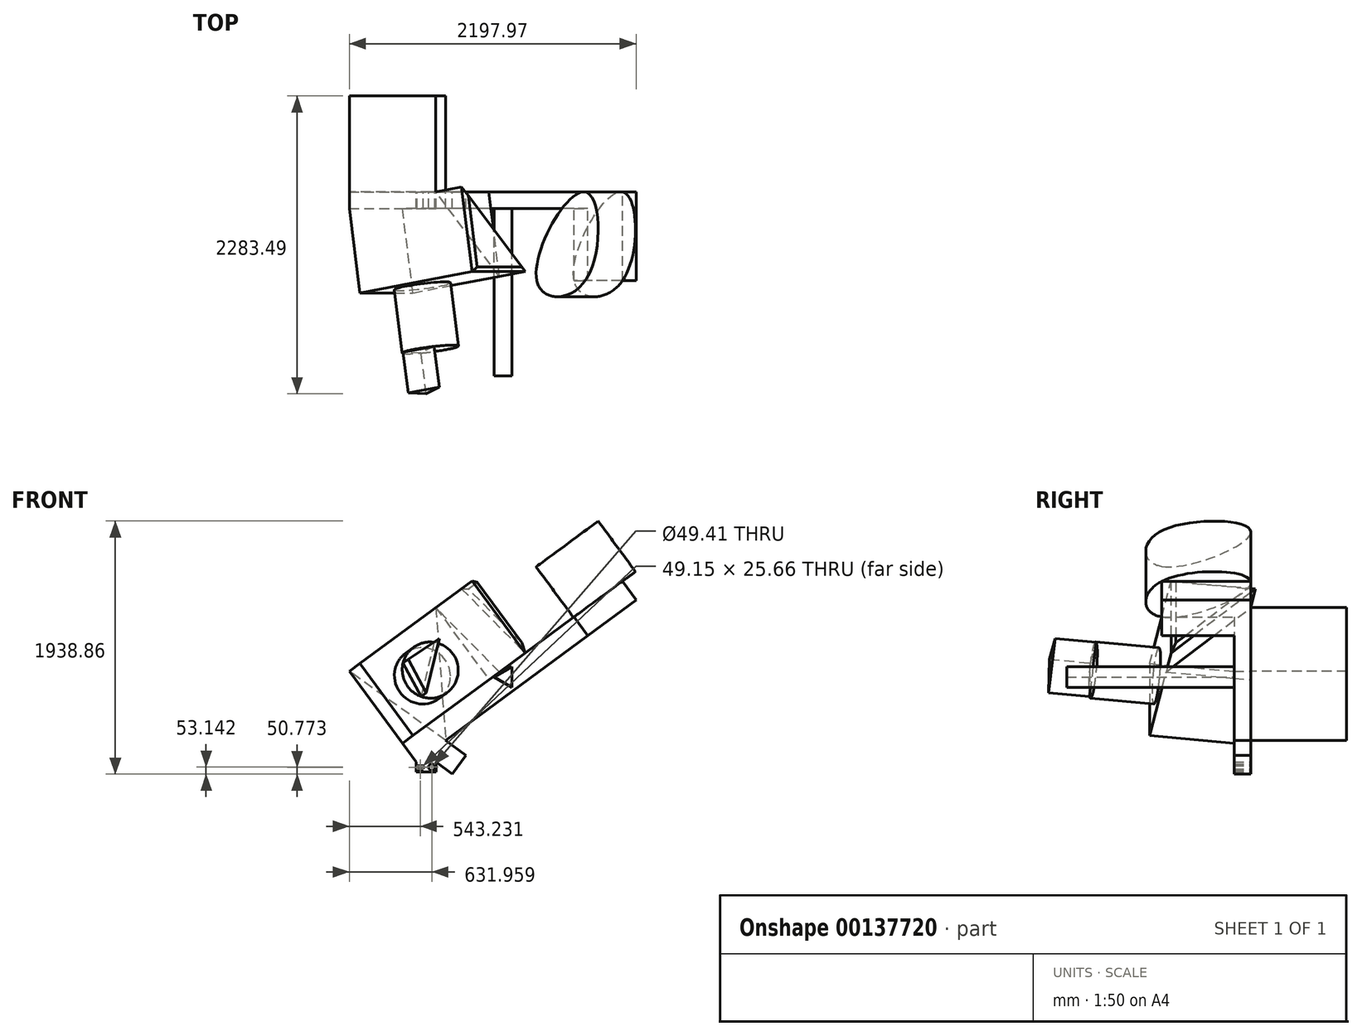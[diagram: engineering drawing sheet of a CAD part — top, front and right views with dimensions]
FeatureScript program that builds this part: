
annotation { "Feature Type Name" : "Feature", "Feature Type Description" : "" }
export const myFeature = defineFeature(function(context is Context, id is Id, definition is map)
    precondition{}
    {
        {
            var Q0;
            Q0=qCreatedBy(makeId("Front.planeOp"),FACE);
            var sketch = newSketch(context, id + "F0", { "sketchPlane" : qUnion([Q0])});
            skLineSegment(sketch, "E0", {"start": v(0, 0) * mm, "end": v(-76.16, 0) * mm});
            skLineSegment(sketch, "E1", {"start": v(-76.16, 0) * mm, "end": v(-76.16, -76.26) * mm});
            skLineSegment(sketch, "E2", {"start": v(-76.16, -76.26) * mm, "end": v(76.16, -76.26) * mm});
            skLineSegment(sketch, "E3", {"start": v(76.16, -76.26) * mm, "end": v(76.16, 0) * mm});
            skLineSegment(sketch, "E4", {"start": v(76.16, 0) * mm, "end": v(0, 0) * mm});
            skLineSegment(sketch, "E5", {"start": v(76.16, 0) * mm, "end": v(0, 56.14) * mm});
            skLineSegment(sketch, "E6", {"start": v(0, 56.14) * mm, "end": v(-76.16, 0) * mm});
            skLineSegment(sketch, "E7", {"start": v(-10.26, -35.22) * mm, "end": v(0, -35.22) * mm});
            skLineSegment(sketch, "E8", {"start": v(0, -35.22) * mm, "end": v(10.26, -35.22) * mm});
            skLineSegment(sketch, "E9", {"start": v(10.26, -35.22) * mm, "end": v(10.26, -76.26) * mm});
            skLineSegment(sketch, "E10", {"start": v(-10.26, -35.22) * mm, "end": v(-10.26, -76.26) * mm});
            skLineSegment(sketch, "E11.bottom", {"start": v(-70.07, -28.36) * mm, "end": v(-20.92, -28.36) * mm});
            skLineSegment(sketch, "E11.top", {"start": v(-70.07, -54.02) * mm, "end": v(-20.92, -54.02) * mm});
            skLineSegment(sketch, "E11.left", {"start": v(-70.07, -28.36) * mm, "end": v(-70.07, -54.02) * mm});
            skLineSegment(sketch, "E11.right", {"start": v(-20.92, -28.36) * mm, "end": v(-20.92, -54.02) * mm});
            skCircle(sketch, "E12", {"center": v(43.23, -38.82) * mm, "radius": 24.7 * mm});
            skSolve(sketch);
        }
        {
            var Q0;
            Q0 = qSketchRegion(id + "F0", true);
            extrude(context, id + "F1", {"entities" : qUnion([Q0]), "depth" : 127 * mm});
        }
        {
            var Q0;
            Q0=makeQuery(id+"F1.opExtrude","SWEPT_FACE",FACE,{"disambiguationData":[OSD([sQuery(id+"F0.wireOp",EDGE,"E5")])]});
            extrude(context, id + "F2", {"entities" : qUnion([Q0]), "operationType" : NewBodyOperationType.ADD, "depth" : 177.8 * mm});
        }
        {
            var Q0;
            Q0=makeQuery(id+"F1.opExtrude","SWEPT_FACE",FACE,{"disambiguationData":[OSD([sQuery(id+"F0.wireOp",EDGE,"E6")])]});
            extrude(context, id + "F3", {"entities" : qUnion([Q0]), "operationType" : NewBodyOperationType.ADD, "depth" : 177.8 * mm});
        }
        {
            var Q0;
            Q0=makeQuery(id+"F3.opExtrude","SWEPT_FACE",FACE,{"disambiguationData":[OSD([sQuery(id+"F0.wireOp",EDGE,"E5"),sQuery(id+"F0.wireOp",EDGE,"E6")])]});
            extrude(context, id + "F4", {"entities" : qUnion([Q0]), "operationType" : NewBodyOperationType.ADD, "depth" : 296.86 * mm});
        }
        {
            var Q0;
            Q0=makeQuery(id+"F2.opExtrude","SWEPT_FACE",FACE,{"disambiguationData":[OSD([sQuery(id+"F0.wireOp",EDGE,"E3"),sQuery(id+"F0.wireOp",EDGE,"E4"),sQuery(id+"F0.wireOp",EDGE,"E5")])]});
            extrude(context, id + "F5", {"entities" : qUnion([Q0]), "operationType" : NewBodyOperationType.ADD, "depth" : 155 * mm});
        }
        {
            var Q0;
            Q0=makeQuery(id+"F4.opExtrude","CAP_FACE",FACE,{"disambiguationData":[OSD([sQuery(id+"F0.wireOp",EDGE,"E5"),sQuery(id+"F0.wireOp",EDGE,"E6")])],"isStart":false});
            extrude(context, id + "F6", {"entities" : qUnion([Q0]), "operationType" : NewBodyOperationType.ADD, "depth" : 1702.25 * mm});
        }
        {
            var Q0;
            {var subQ0=sQuery(id+"F0.wireOp",EDGE,"E6");var subQ1=sQuery(id+"F0.wireOp",EDGE,"E5");var subQ2=makeQuery(id+"F1.opExtrude","CAP_VERTEX",VERTEX,{"disambiguationData":[OSD([subQ1,subQ0])],"isStart":false});var subQ3=makeQuery(id+"F3.opExtrude","SWEPT_EDGE",EDGE,{"disambiguationData":[OSD([subQ1,subQ0]),TDD([makeQuery(id+"F2.boolean.opBoolean","MERGE",VERTEX,{"derivedFrom":[subQ2,makeQuery(id+"F2.opExtrude","CAP_VERTEX",VERTEX,{"disambiguationData":[OSD([subQ1,subQ0]),TDD([subQ2])],"isStart":true})]})])]});var subQ4=sQuery(id+"F0.wireOp",EDGE,"E4");var subQ5=sQuery(id+"F0.wireOp",EDGE,"E3");Q0=makeQuery(id+"F6.boolean.opBoolean","MERGE",FACE,{"derivedFrom":[makeQuery(id+"F5.boolean.opBoolean","MERGE",FACE,{"derivedFrom":[makeQuery(id+"F4.boolean.opBoolean","MERGE",FACE,{"derivedFrom":[makeQuery(id+"F3.boolean.opBoolean","MERGE",FACE,{"derivedFrom":[makeQuery(id+"F2.boolean.opBoolean","MERGE",FACE,{"derivedFrom":[makeQuery(id+"F1.opExtrude","CAP_FACE",FACE,{"disambiguationData":[OSD([sQuery(id+"F0.wireOp",EDGE,"E1"),sQuery(id+"F0.wireOp",EDGE,"E2"),subQ5,subQ1,subQ0,sQuery(id+"F0.wireOp",EDGE,"E11.bottom"),sQuery(id+"F0.wireOp",EDGE,"E11.top"),sQuery(id+"F0.wireOp",EDGE,"E11.left"),sQuery(id+"F0.wireOp",EDGE,"E11.right"),sQuery(id+"F0.wireOp",EDGE,"E12")])],"isStart":false}),makeQuery(id+"F2.opExtrude","SWEPT_FACE",FACE,{"disambiguationData":[OSD([subQ1]),TDD([makeQuery(id+"F1.opExtrude","CAP_EDGE",EDGE,{"disambiguationData":[OSD([subQ1])],"isStart":false})])]})]}),makeQuery(id+"F3.opExtrude","SWEPT_FACE",FACE,{"disambiguationData":[OSD([subQ0]),TDD([makeQuery(id+"F1.opExtrude","CAP_EDGE",EDGE,{"disambiguationData":[OSD([subQ0])],"isStart":false})])]})]}),makeQuery(id+"F4.opExtrude","SWEPT_FACE",FACE,{"disambiguationData":[OSD([subQ1,subQ0]),TDD([subQ3])]})]}),makeQuery(id+"F5.opExtrude","SWEPT_FACE",FACE,{"disambiguationData":[OSD([subQ5,subQ4,subQ1]),TDD([makeQuery(id+"F2.opExtrude","SWEPT_EDGE",EDGE,{"disambiguationData":[OSD([subQ5,subQ4,subQ1]),TDD([makeQuery(id+"F1.opExtrude","CAP_VERTEX",VERTEX,{"disambiguationData":[OSD([subQ5,subQ4,subQ1])],"isStart":false})])]})])]})]}),makeQuery(id+"F6.opExtrude","SWEPT_FACE",FACE,{"disambiguationData":[OSD([subQ1,subQ0]),TDD([makeQuery(id+"F4.opExtrude","CAP_EDGE",EDGE,{"disambiguationData":[OSD([subQ1,subQ0]),TDD([subQ3])],"isStart":false})])]})]});}
            var sketch = newSketch(context, id + "F7", { "sketchPlane" : qUnion([Q0])});
            skLineSegment(sketch, "E13", {"start": v(1134, 1112.82) * mm, "end": v(1239.5, 969.7) * mm});
            skLineSegment(sketch, "E14", {"start": v(1134, 1112.82) * mm, "end": v(1503.75, 1385.34) * mm});
            skLineSegment(sketch, "E15", {"start": v(1503.75, 1385.34) * mm, "end": v(1609.24, 1242.22) * mm});
            skLineSegment(sketch, "E16", {"start": v(1609.24, 1242.22) * mm, "end": v(1239.5, 969.7) * mm});
            skSolve(sketch);
        }
        {
            var Q0;
            Q0 = qSketchRegion(id + "F7", true);
            extrude(context, id + "F8", {"entities" : qUnion([Q0]), "operationType" : NewBodyOperationType.ADD, "depth" : 554.12 * mm});
        }
        {
            var Q0;
            {var subQ0=sQuery(id+"F0.wireOp",EDGE,"E6");var subQ1=sQuery(id+"F0.wireOp",EDGE,"E5");var subQ2=makeQuery(id+"F3.opExtrude","CAP_EDGE",EDGE,{"disambiguationData":[OSD([subQ1,subQ0])],"isStart":false});Q0=makeQuery(id+"F8.boolean.opBoolean","MERGE",FACE,{"derivedFrom":[makeQuery(id+"F6.boolean.opBoolean","MERGE",FACE,{"derivedFrom":[makeQuery(id+"F4.boolean.opBoolean","MERGE",FACE,{"derivedFrom":[makeQuery(id+"F3.opExtrude","CAP_FACE",FACE,{"disambiguationData":[OSD([subQ0])],"isStart":false}),makeQuery(id+"F4.opExtrude","SWEPT_FACE",FACE,{"disambiguationData":[OSD([subQ1,subQ0]),TDD([subQ2])]})]}),makeQuery(id+"F6.opExtrude","SWEPT_FACE",FACE,{"disambiguationData":[OSD([subQ1,subQ0]),TDD([makeQuery(id+"F4.opExtrude","CAP_EDGE",EDGE,{"disambiguationData":[OSD([subQ1,subQ0]),TDD([subQ2])],"isStart":false})])]})]}),makeQuery(id+"F8.opExtrude","SWEPT_FACE",FACE,{"disambiguationData":[OSD([sQuery(id+"F7.wireOp",EDGE,"E14")])]})]});}
            var sketch = newSketch(context, id + "F9", { "sketchPlane" : qUnion([Q0])});
            skLineSegment(sketch, "E17", {"start": v(-61.3, -127) * mm, "end": v(761.56, 0) * mm});
            skLineSegment(sketch, "E18", {"start": v(761.56, 0) * mm, "end": v(-61.3, 0) * mm});
            skLineSegment(sketch, "E19", {"start": v(-61.3, 0) * mm, "end": v(-61.3, -127) * mm});
            skSolve(sketch);
        }
        {
            var Q0;
            Q0 = qSketchRegion(id + "F9", true);
            extrude(context, id + "F10", {"entities" : qUnion([Q0]), "operationType" : NewBodyOperationType.ADD, "depth" : 686.12 * mm});
        }
        {
            var Q0;
            Q0=makeQuery(id+"F10.opExtrude","SWEPT_FACE",FACE,{"disambiguationData":[OSD([sQuery(id+"F9.wireOp",EDGE,"E17")])]});
            extrude(context, id + "F11", {"entities" : qUnion([Q0]), "operationType" : NewBodyOperationType.ADD, "depth" : 654.53 * mm});
        }
        {
            var Q0;
            Q0=makeQuery(id+"F11.opExtrude","SWEPT_FACE",FACE,{"disambiguationData":[OSD([sQuery(id+"F0.wireOp",EDGE,"E5"),sQuery(id+"F0.wireOp",EDGE,"E6"),sQuery(id+"F9.wireOp",EDGE,"E17"),sQuery(id+"F9.wireOp",EDGE,"E18")])]});
            var sketch = newSketch(context, id + "F12", { "sketchPlane" : qUnion([Q0])});
            skLineSegment(sketch, "E20", {"start": v(-770.7, 222.99) * mm, "end": v(-116.16, 909.1) * mm});
            skLineSegment(sketch, "E21", {"start": v(-116.16, 909.1) * mm, "end": v(-770.7, 909.1) * mm});
            skLineSegment(sketch, "E22", {"start": v(-770.7, 909.1) * mm, "end": v(-770.7, 222.99) * mm});
            skSolve(sketch);
        }
        {
            var Q0;
            Q0 = qSketchRegion(id + "F12", true);
            extrude(context, id + "F13", {"entities" : qUnion([Q0]), "operationType" : NewBodyOperationType.ADD, "depth" : 278.87 * mm});
        }
        {
            var Q0;
            Q0=makeQuery(id+"F13.boolean.opBoolean","MERGE",FACE,{"derivedFrom":[makeQuery(id+"F11.opExtrude","CAP_FACE",FACE,{"disambiguationData":[OSD([sQuery(id+"F9.wireOp",EDGE,"E17")])],"isStart":false}),makeQuery(id+"F13.opExtrude","SWEPT_FACE",FACE,{"disambiguationData":[OSD([sQuery(id+"F12.wireOp",EDGE,"E22")])]})]});
            var sketch = newSketch(context, id + "F14", { "sketchPlane" : qUnion([Q0])});
            skCircle(sketch, "E23", {"center": v(-124.02, 591.83) * mm, "radius": 216.26 * mm});
            skSolve(sketch);
        }
        {
            var Q0;
            Q0 = qSketchRegion(id + "F14", true);
            extrude(context, id + "F15", {"entities" : qUnion([Q0]), "operationType" : NewBodyOperationType.ADD, "depth" : 490.5 * mm});
        }
        {
            var Q0;
            Q0=makeQuery(id+"F15.opExtrude","CAP_FACE",FACE,{"disambiguationData":[OSD([sQuery(id+"F14.wireOp",EDGE,"E23")])],"isStart":false});
            var sketch = newSketch(context, id + "F16", { "sketchPlane" : qUnion([Q0])});
            skLineSegment(sketch, "E24", {"start": v(-93.59, 805.94) * mm, "end": v(-194.9, 387.5) * mm});
            skLineSegment(sketch, "E25", {"start": v(-194.9, 387.5) * mm, "end": v(-333.83, 644.26) * mm});
            skLineSegment(sketch, "E26", {"start": v(-333.83, 644.26) * mm, "end": v(-93.59, 805.94) * mm});
            skSolve(sketch);
        }
        {
            var Q0;
            Q0 = qSketchRegion(id + "F16", true);
            extrude(context, id + "F17", {"entities" : qUnion([Q0]), "operationType" : NewBodyOperationType.ADD, "depth" : 316.7 * mm});
        }
        {
            var Q0;
            Q0=makeQuery(id+"F13.opExtrude","CAP_FACE",FACE,{"disambiguationData":[OSD([sQuery(id+"F12.wireOp",EDGE,"E20"),sQuery(id+"F12.wireOp",EDGE,"E21"),sQuery(id+"F12.wireOp",EDGE,"E22")])],"isStart":false});
            chamfer(context, id + "F18", {"entities" : qUnion([Q0]), "width" : 31.04 * mm, "tangentPropagation" : true});
        }
        {
            var Q0;
            {var subQ0=sQuery(id+"F0.wireOp",EDGE,"E6");var subQ1=sQuery(id+"F0.wireOp",EDGE,"E5");var subQ2=makeQuery(id+"F1.opExtrude","CAP_VERTEX",VERTEX,{"disambiguationData":[OSD([subQ1,subQ0])],"isStart":false});var subQ3=makeQuery(id+"F3.opExtrude","SWEPT_EDGE",EDGE,{"disambiguationData":[OSD([subQ1,subQ0]),TDD([makeQuery(id+"F2.boolean.opBoolean","MERGE",VERTEX,{"derivedFrom":[subQ2,makeQuery(id+"F2.opExtrude","CAP_VERTEX",VERTEX,{"disambiguationData":[OSD([subQ1,subQ0]),TDD([subQ2])],"isStart":true})]})])]});var subQ4=sQuery(id+"F0.wireOp",EDGE,"E4");var subQ5=sQuery(id+"F0.wireOp",EDGE,"E3");Q0=makeQuery(id+"F6.boolean.opBoolean","MERGE",FACE,{"derivedFrom":[makeQuery(id+"F5.boolean.opBoolean","MERGE",FACE,{"derivedFrom":[makeQuery(id+"F4.boolean.opBoolean","MERGE",FACE,{"derivedFrom":[makeQuery(id+"F3.boolean.opBoolean","MERGE",FACE,{"derivedFrom":[makeQuery(id+"F2.boolean.opBoolean","MERGE",FACE,{"derivedFrom":[makeQuery(id+"F1.opExtrude","CAP_FACE",FACE,{"disambiguationData":[OSD([sQuery(id+"F0.wireOp",EDGE,"E1"),sQuery(id+"F0.wireOp",EDGE,"E2"),subQ5,subQ1,subQ0,sQuery(id+"F0.wireOp",EDGE,"E11.bottom"),sQuery(id+"F0.wireOp",EDGE,"E11.top"),sQuery(id+"F0.wireOp",EDGE,"E11.left"),sQuery(id+"F0.wireOp",EDGE,"E11.right"),sQuery(id+"F0.wireOp",EDGE,"E12")])],"isStart":false}),makeQuery(id+"F2.opExtrude","SWEPT_FACE",FACE,{"disambiguationData":[OSD([subQ1]),TDD([makeQuery(id+"F1.opExtrude","CAP_EDGE",EDGE,{"disambiguationData":[OSD([subQ1])],"isStart":false})])]})]}),makeQuery(id+"F3.opExtrude","SWEPT_FACE",FACE,{"disambiguationData":[OSD([subQ0]),TDD([makeQuery(id+"F1.opExtrude","CAP_EDGE",EDGE,{"disambiguationData":[OSD([subQ0])],"isStart":false})])]})]}),makeQuery(id+"F4.opExtrude","SWEPT_FACE",FACE,{"disambiguationData":[OSD([subQ1,subQ0]),TDD([subQ3])]})]}),makeQuery(id+"F5.opExtrude","SWEPT_FACE",FACE,{"disambiguationData":[OSD([subQ5,subQ4,subQ1]),TDD([makeQuery(id+"F2.opExtrude","SWEPT_EDGE",EDGE,{"disambiguationData":[OSD([subQ5,subQ4,subQ1]),TDD([makeQuery(id+"F1.opExtrude","CAP_VERTEX",VERTEX,{"disambiguationData":[OSD([subQ5,subQ4,subQ1])],"isStart":false})])]})])]})]}),makeQuery(id+"F6.opExtrude","SWEPT_FACE",FACE,{"disambiguationData":[OSD([subQ1,subQ0]),TDD([makeQuery(id+"F4.opExtrude","CAP_EDGE",EDGE,{"disambiguationData":[OSD([subQ1,subQ0]),TDD([subQ3])],"isStart":false})])]})]});}
            var sketch = newSketch(context, id + "F19", { "sketchPlane" : qUnion([Q0])});
            skCircle(sketch, "E27.cCircle", {"center": v(612.36, 650.54) * mm, "radius": 45.96 * mm, "construction": true});
            skLineSegment(sketch, "E27.0", {"start": v(658.32, 730.15) * mm, "end": v(658.32, 570.93) * mm});
            skLineSegment(sketch, "E27.1", {"start": v(658.32, 570.93) * mm, "end": v(520.43, 650.54) * mm});
            skLineSegment(sketch, "E27.2", {"start": v(520.43, 650.54) * mm, "end": v(658.32, 730.15) * mm});
            skPoint(sketch, "E27.0.midPoint", {"position": v(658.32, 650.54) * mm});
            skSolve(sketch);
        }
        {
            var Q0;
            Q0 = qSketchRegion(id + "F19", true);
            extrude(context, id + "F20", {"entities" : qUnion([Q0]), "operationType" : NewBodyOperationType.ADD, "depth" : 1281.9 * mm});
        }
        {
            var Q0;
            {var subQ0=sQuery(id+"F0.wireOp",EDGE,"E6");var subQ1=sQuery(id+"F0.wireOp",EDGE,"E5");var subQ2=makeQuery(id+"F1.opExtrude","CAP_VERTEX",VERTEX,{"disambiguationData":[OSD([subQ1,subQ0])],"isStart":true});var subQ3=makeQuery(id+"F3.opExtrude","SWEPT_EDGE",EDGE,{"disambiguationData":[OSD([subQ1,subQ0]),TDD([makeQuery(id+"F2.boolean.opBoolean","MERGE",VERTEX,{"derivedFrom":[subQ2,makeQuery(id+"F2.opExtrude","CAP_VERTEX",VERTEX,{"disambiguationData":[OSD([subQ1,subQ0]),TDD([subQ2])],"isStart":true})]})])]});var subQ4=sQuery(id+"F0.wireOp",EDGE,"E4");var subQ5=sQuery(id+"F0.wireOp",EDGE,"E3");Q0=makeQuery(id+"F10.boolean.opBoolean","MERGE",FACE,{"derivedFrom":[makeQuery(id+"F6.boolean.opBoolean","MERGE",FACE,{"derivedFrom":[makeQuery(id+"F5.boolean.opBoolean","MERGE",FACE,{"derivedFrom":[makeQuery(id+"F4.boolean.opBoolean","MERGE",FACE,{"derivedFrom":[makeQuery(id+"F3.boolean.opBoolean","MERGE",FACE,{"derivedFrom":[makeQuery(id+"F2.boolean.opBoolean","MERGE",FACE,{"derivedFrom":[makeQuery(id+"F1.opExtrude","CAP_FACE",FACE,{"disambiguationData":[OSD([sQuery(id+"F0.wireOp",EDGE,"E1"),sQuery(id+"F0.wireOp",EDGE,"E2"),subQ5,subQ1,subQ0,sQuery(id+"F0.wireOp",EDGE,"E11.bottom"),sQuery(id+"F0.wireOp",EDGE,"E11.top"),sQuery(id+"F0.wireOp",EDGE,"E11.left"),sQuery(id+"F0.wireOp",EDGE,"E11.right"),sQuery(id+"F0.wireOp",EDGE,"E12")])],"isStart":true}),makeQuery(id+"F2.opExtrude","SWEPT_FACE",FACE,{"disambiguationData":[OSD([subQ1]),TDD([makeQuery(id+"F1.opExtrude","CAP_EDGE",EDGE,{"disambiguationData":[OSD([subQ1])],"isStart":true})])]})]}),makeQuery(id+"F3.opExtrude","SWEPT_FACE",FACE,{"disambiguationData":[OSD([subQ0]),TDD([makeQuery(id+"F1.opExtrude","CAP_EDGE",EDGE,{"disambiguationData":[OSD([subQ0])],"isStart":true})])]})]}),makeQuery(id+"F4.opExtrude","SWEPT_FACE",FACE,{"disambiguationData":[OSD([subQ1,subQ0]),TDD([subQ3])]})]}),makeQuery(id+"F5.opExtrude","SWEPT_FACE",FACE,{"disambiguationData":[OSD([subQ5,subQ4,subQ1]),TDD([makeQuery(id+"F2.opExtrude","SWEPT_EDGE",EDGE,{"disambiguationData":[OSD([subQ5,subQ4,subQ1]),TDD([makeQuery(id+"F1.opExtrude","CAP_VERTEX",VERTEX,{"disambiguationData":[OSD([subQ5,subQ4,subQ1])],"isStart":true})])]})])]})]}),makeQuery(id+"F6.opExtrude","SWEPT_FACE",FACE,{"disambiguationData":[OSD([subQ1,subQ0]),TDD([makeQuery(id+"F4.opExtrude","CAP_EDGE",EDGE,{"disambiguationData":[OSD([subQ1,subQ0]),TDD([subQ3])],"isStart":false})])]})]}),makeQuery(id+"F10.opExtrude","SWEPT_FACE",FACE,{"disambiguationData":[OSD([sQuery(id+"F9.wireOp",EDGE,"E18")])]})]});}
            var sketch = newSketch(context, id + "F21", { "sketchPlane" : qUnion([Q0])});
            skLineSegment(sketch, "E28", {"start": v(-73.66, 1183.65) * mm, "end": v(-149.84, 166.57) * mm});
            skLineSegment(sketch, "E29", {"start": v(-149.84, 166.57) * mm, "end": v(588.73, 695.44) * mm});
            skLineSegment(sketch, "E30", {"start": v(588.73, 695.44) * mm, "end": v(-73.66, 1183.65) * mm});
            skSolve(sketch);
        }
        {
            var Q0;
            Q0 = qSketchRegion(id + "F21", true);
            extrude(context, id + "F22", {"entities" : qUnion([Q0]), "operationType" : NewBodyOperationType.ADD, "depth" : 735.57 * mm});
        }
        {
            var Q0;
            {var subQ0=sQuery(id+"F0.wireOp",EDGE,"E6");var subQ1=sQuery(id+"F0.wireOp",EDGE,"E5");var subQ2=makeQuery(id+"F3.opExtrude","CAP_EDGE",EDGE,{"disambiguationData":[OSD([subQ1,subQ0])],"isStart":false});Q0=makeQuery(id+"F8.boolean.opBoolean","MERGE",FACE,{"derivedFrom":[makeQuery(id+"F6.boolean.opBoolean","MERGE",FACE,{"derivedFrom":[makeQuery(id+"F4.boolean.opBoolean","MERGE",FACE,{"derivedFrom":[makeQuery(id+"F3.opExtrude","CAP_FACE",FACE,{"disambiguationData":[OSD([subQ0])],"isStart":false}),makeQuery(id+"F4.opExtrude","SWEPT_FACE",FACE,{"disambiguationData":[OSD([subQ1,subQ0]),TDD([subQ2])]})]}),makeQuery(id+"F6.opExtrude","SWEPT_FACE",FACE,{"disambiguationData":[OSD([subQ1,subQ0]),TDD([makeQuery(id+"F4.opExtrude","CAP_EDGE",EDGE,{"disambiguationData":[OSD([subQ1,subQ0]),TDD([subQ2])],"isStart":false})])]})]}),makeQuery(id+"F8.opExtrude","SWEPT_FACE",FACE,{"disambiguationData":[OSD([sQuery(id+"F7.wireOp",EDGE,"E14")])]})]});}
            var sketch = newSketch(context, id + "F23", { "sketchPlane" : qUnion([Q0])});
            skFitSpline(sketch, "E31", {"points": [v(1573.1, -681.12) * mm, v(2032.42, 0) * mm, v(2032.42, -681.12) * mm, v(1573.1, -681.12) * mm]});
            skSolve(sketch);
        }
        {
            var Q0;
            Q0 = qSketchRegion(id + "F23", true);
            extrude(context, id + "F24", {"entities" : qUnion([Q0]), "operationType" : NewBodyOperationType.ADD, "depth" : 481.42 * mm});
        }
    });
